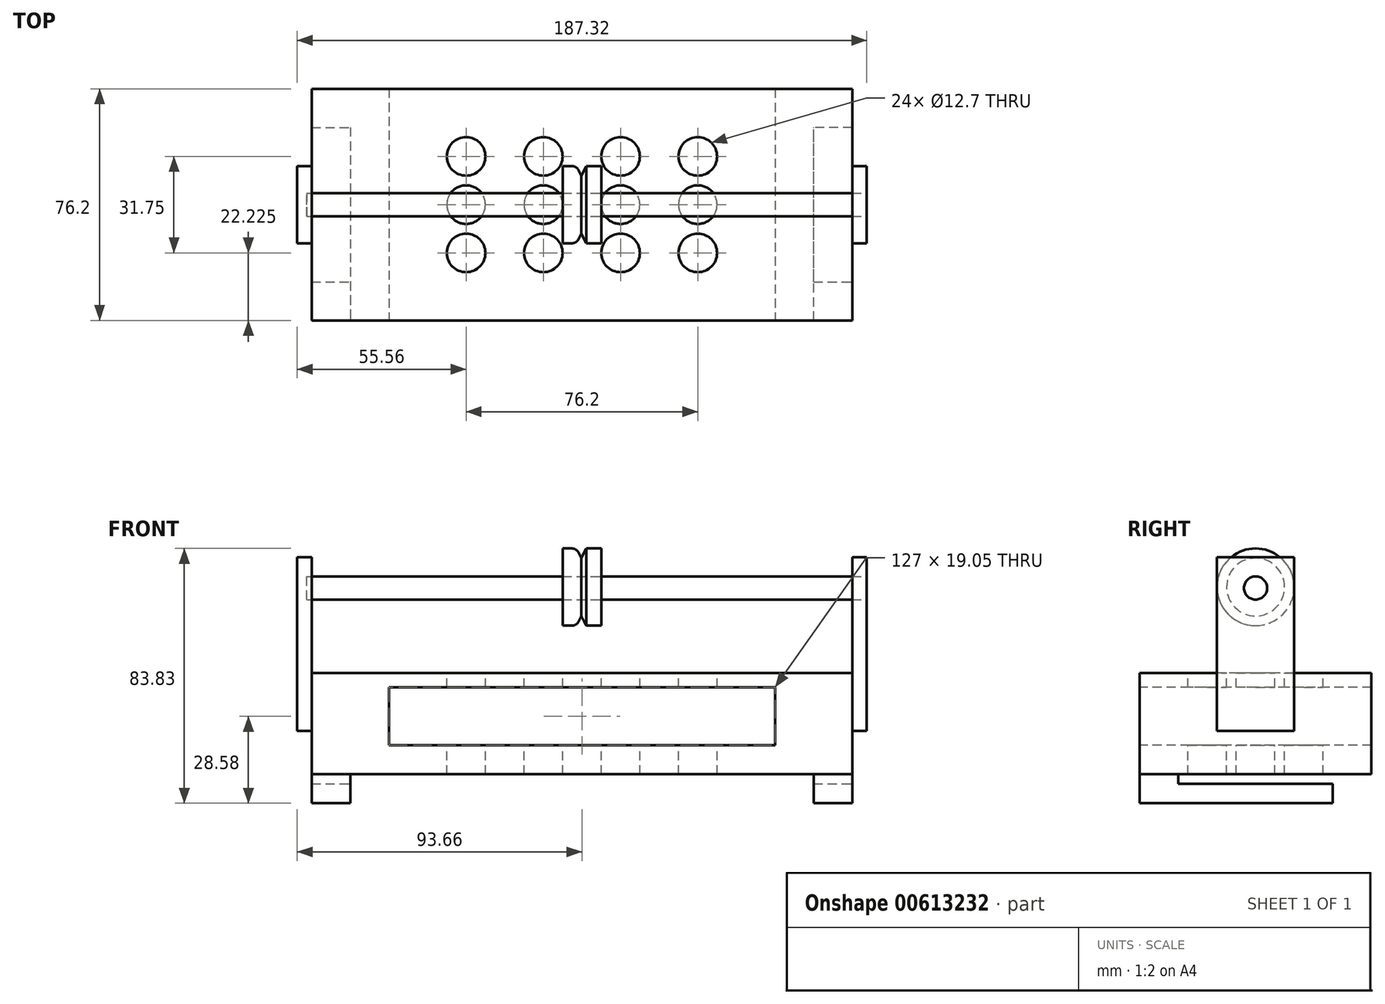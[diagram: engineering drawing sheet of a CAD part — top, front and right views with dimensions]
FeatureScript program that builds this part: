
annotation { "Feature Type Name" : "Feature", "Feature Type Description" : "" }
export const myFeature = defineFeature(function(context is Context, id is Id, definition is map)
    precondition{}
    {
        {
            var Q0;
            Q0=qCreatedBy(makeId("Front.planeOp"),FACE);
            var sketch = newSketch(context, id + "F0", { "sketchPlane" : qUnion([Q0])});
            skLineSegment(sketch, "E0", {"start": v(0, 0) * mm, "end": v(0, 33.34) * mm});
            skLineSegment(sketch, "E1", {"start": v(0, 33.34) * mm, "end": v(177.8, 33.34) * mm});
            skLineSegment(sketch, "E2", {"start": v(177.8, 33.34) * mm, "end": v(177.8, 0) * mm});
            skLineSegment(sketch, "E3", {"start": v(25.4, 28.58) * mm, "end": v(152.4, 28.58) * mm});
            skLineSegment(sketch, "E4", {"start": v(0, 0) * mm, "end": v(177.8, 0) * mm});
            skLineSegment(sketch, "E5", {"start": v(0, 9.52) * mm, "end": v(177.8, 9.53) * mm});
            skLineSegment(sketch, "E6", {"start": v(25.4, 28.58) * mm, "end": v(25.4, 9.52) * mm});
            skLineSegment(sketch, "E7", {"start": v(152.4, 28.58) * mm, "end": v(152.4, 9.53) * mm});
            skSolve(sketch);
        }
        {
            var Q0;
            {var subQ1=sQuery(id+"F0.wireOp",EDGE,"E1");Q0=makeQuery(id+"F0.imprint","IMPRINT",FACE,{"disambiguationData":[TD([[makeQuery(id+"F0.imprint","IMPRINT",EDGE,{"derivedFrom":subQ1}),-1.0]])]});}
            var Q1;
            {var subQ4=sQuery(id+"F0.wireOp",EDGE,"E4");Q1=makeQuery(id+"F0.imprint","IMPRINT",FACE,{"disambiguationData":[TD([[makeQuery(id+"F0.imprint","IMPRINT",EDGE,{"derivedFrom":subQ4}),1.0]])]});}
            var Q2;
            Q2=makeQuery(id+"F0.imprint","IMPRINT",FACE,{"disambiguationData":[TD([[makeQuery(id+"F0.imprint","IMPRINT",EDGE,{"derivedFrom":sQuery(id+"F0.wireOp",EDGE,"E3")}),-1.0]])]});
            extrude(context, id + "F1", {"entities" : qUnion([Q0, Q1, Q2]), "oppositeDirection" : true, "depth" : 76.2 * mm, "offsetDistance" : 25.4 * mm});
        }
        {
            var Q0;
            Q0=makeQuery(id+"F0.imprint","IMPRINT",FACE,{"disambiguationData":[TD([[makeQuery(id+"F0.imprint","IMPRINT",EDGE,{"derivedFrom":sQuery(id+"F0.wireOp",EDGE,"E3")}),-1.0]])]});
            extrude(context, id + "F2", {"entities" : qUnion([Q0]), "operationType" : NewBodyOperationType.REMOVE, "oppositeDirection" : true, "depth" : 76.2 * mm, "offsetDistance" : 25.4 * mm});
        }
        {
            var Q0;
            Q0=makeQuery(id+"F1.opExtrude","SWEPT_FACE",FACE,{"disambiguationData":[OSD([sQuery(id+"F0.wireOp",EDGE,"E2")])]});
            var sketch = newSketch(context, id + "F3", { "sketchPlane" : qUnion([Q0])});
            skLineSegment(sketch, "E8", {"start": v(0, 33.34) * mm, "end": v(25.4, 33.34) * mm});
            skLineSegment(sketch, "E9", {"start": v(76.2, 33.34) * mm, "end": v(50.8, 33.34) * mm});
            skLineSegment(sketch, "E10", {"start": v(50.8, 33.34) * mm, "end": v(50.8, 71.44) * mm});
            skLineSegment(sketch, "E11", {"start": v(50.8, 71.44) * mm, "end": v(25.4, 71.44) * mm});
            skLineSegment(sketch, "E12", {"start": v(25.4, 71.44) * mm, "end": v(25.4, 33.34) * mm});
            skLineSegment(sketch, "E13", {"start": v(25.4, 33.34) * mm, "end": v(25.4, 14.29) * mm});
            skLineSegment(sketch, "E14", {"start": v(25.4, 14.29) * mm, "end": v(50.8, 14.29) * mm});
            skLineSegment(sketch, "E15", {"start": v(50.8, 14.29) * mm, "end": v(50.8, 33.34) * mm});
            skSolve(sketch);
        }
        {
            var Q0;
            {var subQ0=sQuery(id+"F3.wireOp",EDGE,"E13");Q0=makeQuery(id+"F3.imprint","IMPRINT",FACE,{"disambiguationData":[TD([[makeQuery(id+"F3.imprint","IMPRINT",EDGE,{"derivedFrom":subQ0}),1.0]])]});}
            var Q1;
            {var subQ0=sQuery(id+"F3.wireOp",EDGE,"E10");Q1=makeQuery(id+"F3.imprint","IMPRINT",FACE,{"disambiguationData":[TD([[makeQuery(id+"F3.imprint","IMPRINT",EDGE,{"derivedFrom":subQ0}),1.0]])]});}
            extrude(context, id + "F4", {"entities" : qUnion([Q0, Q1]), "operationType" : NewBodyOperationType.ADD, "depth" : 4.76 * mm, "offsetDistance" : 25.4 * mm});
        }
        {
            var Q0;
            Q0=makeQuery(id+"F1.opExtrude","SWEPT_FACE",FACE,{"disambiguationData":[OSD([sQuery(id+"F0.wireOp",EDGE,"E0")])]});
            var sketch = newSketch(context, id + "F5", { "sketchPlane" : qUnion([Q0])});
            skLineSegment(sketch, "E16", {"start": v(-76.2, 33.34) * mm, "end": v(-50.8, 33.34) * mm});
            skLineSegment(sketch, "E17", {"start": v(-50.8, 33.34) * mm, "end": v(-50.8, 71.44) * mm});
            skLineSegment(sketch, "E18", {"start": v(-50.8, 71.44) * mm, "end": v(-25.4, 71.44) * mm});
            skLineSegment(sketch, "E19", {"start": v(-25.4, 71.44) * mm, "end": v(-25.4, 33.34) * mm});
            skLineSegment(sketch, "E20", {"start": v(-25.4, 33.34) * mm, "end": v(0, 33.34) * mm});
            skLineSegment(sketch, "E21", {"start": v(-50.8, 33.34) * mm, "end": v(-50.8, 14.29) * mm});
            skLineSegment(sketch, "E22", {"start": v(-50.8, 14.29) * mm, "end": v(-25.4, 14.29) * mm});
            skLineSegment(sketch, "E23", {"start": v(-25.4, 14.29) * mm, "end": v(-25.4, 33.34) * mm});
            skSolve(sketch);
        }
        {
            var Q0;
            {var subQ0=sQuery(id+"F5.wireOp",EDGE,"E17");Q0=makeQuery(id+"F5.imprint","IMPRINT",FACE,{"disambiguationData":[TD([[makeQuery(id+"F5.imprint","IMPRINT",EDGE,{"derivedFrom":subQ0}),-1.0]])]});}
            var Q1;
            {var subQ0=sQuery(id+"F5.wireOp",EDGE,"E21");Q1=makeQuery(id+"F5.imprint","IMPRINT",FACE,{"disambiguationData":[TD([[makeQuery(id+"F5.imprint","IMPRINT",EDGE,{"derivedFrom":subQ0}),1.0]])]});}
            extrude(context, id + "F6", {"entities" : qUnion([Q0, Q1]), "operationType" : NewBodyOperationType.ADD, "depth" : 4.76 * mm, "offsetDistance" : 25.4 * mm});
        }
        {
            var Q0;
            Q0=makeQuery(id+"F1.opExtrude","SWEPT_FACE",FACE,{"disambiguationData":[OSD([sQuery(id+"F0.wireOp",EDGE,"E1")])]});
            var sketch = newSketch(context, id + "F7", { "sketchPlane" : qUnion([Q0])});
            skLineSegment(sketch, "E24", {"start": v(0, 0) * mm, "end": v(0, 76.2) * mm});
            skLineSegment(sketch, "E25", {"start": v(177.8, 76.2) * mm, "end": v(177.8, 0) * mm});
            skCircle(sketch, "E26", {"center": v(50.8, 53.98) * mm, "radius": 6.35 * mm});
            skCircle(sketch, "E27", {"center": v(50.8, 38.1) * mm, "radius": 6.35 * mm});
            skCircle(sketch, "E28", {"center": v(50.8, 22.22) * mm, "radius": 6.35 * mm});
            skCircle(sketch, "E29", {"center": v(76.2, 38.1) * mm, "radius": 6.35 * mm});
            skCircle(sketch, "E30", {"center": v(76.2, 53.98) * mm, "radius": 6.35 * mm});
            skCircle(sketch, "E31", {"center": v(76.2, 22.22) * mm, "radius": 6.35 * mm});
            skCircle(sketch, "E32", {"center": v(101.6, 38.1) * mm, "radius": 6.35 * mm});
            skCircle(sketch, "E33", {"center": v(101.6, 53.98) * mm, "radius": 6.35 * mm});
            skCircle(sketch, "E34", {"center": v(101.6, 22.22) * mm, "radius": 6.35 * mm});
            skCircle(sketch, "E35", {"center": v(127, 22.22) * mm, "radius": 6.35 * mm});
            skCircle(sketch, "E36", {"center": v(127, 53.98) * mm, "radius": 6.35 * mm});
            skCircle(sketch, "E37", {"center": v(127, 38.1) * mm, "radius": 6.35 * mm});
            skSolve(sketch);
        }
        {
            var Q0;
            Q0=makeQuery(id+"F7.imprint","IMPRINT",FACE,{"disambiguationData":[TD([[makeQuery(id+"F7.imprint","IMPRINT",EDGE,{"derivedFrom":sQuery(id+"F7.wireOp",EDGE,"E26")}),1.0]])]});
            var Q1;
            Q1=makeQuery(id+"F7.imprint","IMPRINT",FACE,{"disambiguationData":[TD([[makeQuery(id+"F7.imprint","IMPRINT",EDGE,{"derivedFrom":sQuery(id+"F7.wireOp",EDGE,"E27")}),1.0]])]});
            var Q2;
            Q2=makeQuery(id+"F7.imprint","IMPRINT",FACE,{"disambiguationData":[TD([[makeQuery(id+"F7.imprint","IMPRINT",EDGE,{"derivedFrom":sQuery(id+"F7.wireOp",EDGE,"E28")}),1.0]])]});
            var Q3;
            Q3=makeQuery(id+"F7.imprint","IMPRINT",FACE,{"disambiguationData":[TD([[makeQuery(id+"F7.imprint","IMPRINT",EDGE,{"derivedFrom":sQuery(id+"F7.wireOp",EDGE,"E31")}),1.0]])]});
            var Q4;
            Q4=makeQuery(id+"F7.imprint","IMPRINT",FACE,{"disambiguationData":[TD([[makeQuery(id+"F7.imprint","IMPRINT",EDGE,{"derivedFrom":sQuery(id+"F7.wireOp",EDGE,"E29")}),1.0]])]});
            var Q5;
            Q5=makeQuery(id+"F7.imprint","IMPRINT",FACE,{"disambiguationData":[TD([[makeQuery(id+"F7.imprint","IMPRINT",EDGE,{"derivedFrom":sQuery(id+"F7.wireOp",EDGE,"E30")}),1.0]])]});
            var Q6;
            Q6=makeQuery(id+"F7.imprint","IMPRINT",FACE,{"disambiguationData":[TD([[makeQuery(id+"F7.imprint","IMPRINT",EDGE,{"derivedFrom":sQuery(id+"F7.wireOp",EDGE,"E33")}),1.0]])]});
            var Q7;
            Q7=makeQuery(id+"F7.imprint","IMPRINT",FACE,{"disambiguationData":[TD([[makeQuery(id+"F7.imprint","IMPRINT",EDGE,{"derivedFrom":sQuery(id+"F7.wireOp",EDGE,"E32")}),1.0]])]});
            var Q8;
            Q8=makeQuery(id+"F7.imprint","IMPRINT",FACE,{"disambiguationData":[TD([[makeQuery(id+"F7.imprint","IMPRINT",EDGE,{"derivedFrom":sQuery(id+"F7.wireOp",EDGE,"E34")}),1.0]])]});
            var Q9;
            Q9=makeQuery(id+"F7.imprint","IMPRINT",FACE,{"disambiguationData":[TD([[makeQuery(id+"F7.imprint","IMPRINT",EDGE,{"derivedFrom":sQuery(id+"F7.wireOp",EDGE,"E35")}),1.0]])]});
            var Q10;
            Q10=makeQuery(id+"F7.imprint","IMPRINT",FACE,{"disambiguationData":[TD([[makeQuery(id+"F7.imprint","IMPRINT",EDGE,{"derivedFrom":sQuery(id+"F7.wireOp",EDGE,"E37")}),1.0]])]});
            var Q11;
            Q11=makeQuery(id+"F7.imprint","IMPRINT",FACE,{"disambiguationData":[TD([[makeQuery(id+"F7.imprint","IMPRINT",EDGE,{"derivedFrom":sQuery(id+"F7.wireOp",EDGE,"E36")}),1.0]])]});
            extrude(context, id + "F8", {"entities" : qUnion([Q0, Q1, Q2, Q3, Q4, Q5, Q6, Q7, Q8, Q9, Q10, Q11]), "operationType" : NewBodyOperationType.REMOVE, "oppositeDirection" : true, "depth" : 34.3 * mm, "offsetDistance" : 25.4 * mm});
        }
        {
            var Q0;
            Q0=makeQuery(id+"F4.opExtrude","CAP_FACE",FACE,{"disambiguationData":[OSD([sQuery(id+"F3.wireOp",EDGE,"E10"),sQuery(id+"F3.wireOp",EDGE,"E11"),sQuery(id+"F3.wireOp",EDGE,"E12"),sQuery(id+"F3.wireOp",EDGE,"E13"),sQuery(id+"F3.wireOp",EDGE,"E14"),sQuery(id+"F3.wireOp",EDGE,"E15")])],"isStart":false});
            var sketch = newSketch(context, id + "F9", { "sketchPlane" : qUnion([Q0])});
            skCircle(sketch, "E38", {"center": v(38.1, 61.28) * mm, "radius": 3.81 * mm});
            skSolve(sketch);
        }
        {
            var Q0;
            Q0=makeQuery(id+"F9.imprint","IMPRINT",FACE,{"disambiguationData":[TD([[makeQuery(id+"F9.imprint","IMPRINT",EDGE,{"derivedFrom":sQuery(id+"F9.wireOp",EDGE,"E38")}),1.0]])]});
            extrude(context, id + "F10", {"entities" : qUnion([Q0]), "oppositeDirection" : true, "depth" : 184.15 * mm, "offsetDistance" : 25.4 * mm});
        }
        {
            var Q0;
            Q0=makeQuery(id+"F1.opExtrude","SWEPT_FACE",FACE,{"disambiguationData":[OSD([sQuery(id+"F0.wireOp",EDGE,"E4")])]});
            var sketch = newSketch(context, id + "F11", { "sketchPlane" : qUnion([Q0])});
            skLineSegment(sketch, "E39", {"start": v(0, 0) * mm, "end": v(0, -12.7) * mm});
            skLineSegment(sketch, "E40", {"start": v(0, -12.7) * mm, "end": v(12.7, -12.7) * mm});
            skLineSegment(sketch, "E41", {"start": v(12.7, -12.7) * mm, "end": v(12.7, 0) * mm});
            skLineSegment(sketch, "E42", {"start": v(12.7, 0) * mm, "end": v(0, 0) * mm});
            skLineSegment(sketch, "E43", {"start": v(177.8, 0) * mm, "end": v(165.1, 0) * mm});
            skLineSegment(sketch, "E44", {"start": v(165.1, 0) * mm, "end": v(165.1, -12.7) * mm});
            skLineSegment(sketch, "E45", {"start": v(165.1, -12.7) * mm, "end": v(177.8, -12.7) * mm});
            skLineSegment(sketch, "E46", {"start": v(177.8, -12.7) * mm, "end": v(177.8, 0) * mm});
            skSolve(sketch);
        }
        {
            var Q0;
            Q0=makeQuery(id+"F11.imprint","IMPRINT",FACE,{"disambiguationData":[TD([[makeQuery(id+"F11.imprint","IMPRINT",EDGE,{"derivedFrom":sQuery(id+"F11.wireOp",EDGE,"E39")}),-1.0]])]});
            var Q1;
            Q1=makeQuery(id+"F11.imprint","IMPRINT",FACE,{"disambiguationData":[TD([[makeQuery(id+"F11.imprint","IMPRINT",EDGE,{"derivedFrom":sQuery(id+"F11.wireOp",EDGE,"E43")}),-1.0]])]});
            extrude(context, id + "F12", {"entities" : qUnion([Q0, Q1]), "depth" : 3.17 * mm, "offsetDistance" : 25.4 * mm});
        }
        {
            var Q0;
            Q0=makeQuery(id+"F12.opExtrude","CAP_FACE",FACE,{"disambiguationData":[OSD([sQuery(id+"F11.wireOp",EDGE,"E39"),sQuery(id+"F11.wireOp",EDGE,"E40"),sQuery(id+"F11.wireOp",EDGE,"E41"),sQuery(id+"F11.wireOp",EDGE,"E42")])],"isStart":false});
            var sketch = newSketch(context, id + "F13", { "sketchPlane" : qUnion([Q0])});
            skLineSegment(sketch, "E47", {"start": v(0, 0) * mm, "end": v(0, -63.5) * mm});
            skLineSegment(sketch, "E48", {"start": v(0, -63.5) * mm, "end": v(12.7, -63.5) * mm});
            skLineSegment(sketch, "E49", {"start": v(12.7, -63.5) * mm, "end": v(12.7, 0) * mm});
            skLineSegment(sketch, "E50", {"start": v(12.7, 0) * mm, "end": v(0, 0) * mm});
            skSolve(sketch);
        }
        {
            var Q0;
            {var subQ2=sQuery(id+"F13.wireOp",EDGE,"E48");Q0=makeQuery(id+"F13.imprint","IMPRINT",FACE,{"disambiguationData":[TD([[makeQuery(id+"F13.imprint","IMPRINT",EDGE,{"derivedFrom":subQ2}),1.0]])]});}
            var Q1;
            {var subQ0=sQuery(id+"F13.wireOp",EDGE,"E50");Q1=makeQuery(id+"F13.imprint","IMPRINT",FACE,{"disambiguationData":[TD([[makeQuery(id+"F13.imprint","IMPRINT",EDGE,{"derivedFrom":subQ0}),-1.0]])]});}
            extrude(context, id + "F14", {"entities" : qUnion([Q0, Q1]), "operationType" : NewBodyOperationType.ADD, "depth" : 6.35 * mm, "offsetDistance" : 25.4 * mm});
        }
        {
            var Q0;
            Q0=makeQuery(id+"F12.opExtrude","CAP_FACE",FACE,{"disambiguationData":[OSD([sQuery(id+"F11.wireOp",EDGE,"E43"),sQuery(id+"F11.wireOp",EDGE,"E44"),sQuery(id+"F11.wireOp",EDGE,"E45"),sQuery(id+"F11.wireOp",EDGE,"E46")])],"isStart":false});
            var sketch = newSketch(context, id + "F15", { "sketchPlane" : qUnion([Q0])});
            skLineSegment(sketch, "E51", {"start": v(177.8, 0) * mm, "end": v(177.8, -63.5) * mm});
            skLineSegment(sketch, "E52", {"start": v(177.8, -63.5) * mm, "end": v(165.1, -63.5) * mm});
            skLineSegment(sketch, "E53", {"start": v(165.1, -63.5) * mm, "end": v(165.1, 0) * mm});
            skLineSegment(sketch, "E54", {"start": v(165.1, 0) * mm, "end": v(177.8, 0) * mm});
            skSolve(sketch);
        }
        {
            var Q0;
            {var subQ0=sQuery(id+"F15.wireOp",EDGE,"E54");Q0=makeQuery(id+"F15.imprint","IMPRINT",FACE,{"disambiguationData":[TD([[makeQuery(id+"F15.imprint","IMPRINT",EDGE,{"derivedFrom":subQ0}),-1.0]])]});}
            var Q1;
            {var subQ2=sQuery(id+"F15.wireOp",EDGE,"E52");Q1=makeQuery(id+"F15.imprint","IMPRINT",FACE,{"disambiguationData":[TD([[makeQuery(id+"F15.imprint","IMPRINT",EDGE,{"derivedFrom":subQ2}),-1.0]])]});}
            extrude(context, id + "F16", {"entities" : qUnion([Q0, Q1]), "operationType" : NewBodyOperationType.ADD, "depth" : 6.35 * mm, "offsetDistance" : 25.4 * mm});
        }
        {
            var Q0;
            Q0=qCreatedBy(makeId("Right.planeOp"),FACE);
            cPlane(context, id + "F17", {"entities" : qUnion([Q0]), "cplaneType" : CPlaneType.OFFSET, "offset" : 88.9 * mm, "width" : 152.4 * mm, "height" : 152.4 * mm});
        }
        {
            var Q0;
            Q0=qCreatedBy(id+"F17.planeOp",FACE);
            var sketch = newSketch(context, id + "F18", { "sketchPlane" : qUnion([Q0])});
            skCircle(sketch, "E55", {"center": v(38.1, 61.6) * mm, "radius": 12.7 * mm});
            skSolve(sketch);
        }
        {
            var Q0;
            Q0=makeQuery(id+"F18.imprint","IMPRINT",FACE,{"disambiguationData":[TD([[makeQuery(id+"F18.imprint","IMPRINT",EDGE,{"derivedFrom":sQuery(id+"F18.wireOp",EDGE,"E55")}),1.0]])]});
            extrude(context, id + "F19", {"entities" : qUnion([Q0]), "endBound" : BoundingType.SYMMETRIC, "depth" : 12.7 * mm, "offsetDistance" : 25.4 * mm});
        }
        {
            var Q0;
            Q0=qCreatedBy(makeId("Front.planeOp"),FACE);
            cPlane(context, id + "F20", {"entities" : qUnion([Q0]), "cplaneType" : CPlaneType.OFFSET, "offset" : 38.1 * mm, "oppositeDirection" : true, "width" : 152.4 * mm, "height" : 152.4 * mm});
        }
        {
            var Q0;
            Q0=qCreatedBy(id+"F20.planeOp",FACE);
            var sketch = newSketch(context, id + "F21", { "sketchPlane" : qUnion([Q0])});
            skLineSegment(sketch, "E56.0", {"start": v(82.55, 74.3) * mm, "end": v(82.55, 48.9) * mm});
            skLineSegment(sketch, "E57.0", {"start": v(95.25, 74.3) * mm, "end": v(95.25, 48.9) * mm});
            skLineSegment(sketch, "E58", {"start": v(87.12, 74.3) * mm, "end": v(90.3, 74.3) * mm});
            skLineSegment(sketch, "E59", {"start": v(82.55, 61.6) * mm, "end": v(95.25, 61.6) * mm});
            skLineSegment(sketch, "E60", {"start": v(87.12, 74.3) * mm, "end": v(88.7, 71.12) * mm});
            skPoint(sketch, "E60.endSnap0", {"position": v(88.7, 74.3) * mm});
            skLineSegment(sketch, "E61", {"start": v(88.7, 71.12) * mm, "end": v(90.3, 74.3) * mm});
            skSolve(sketch);
        }
        {
            var Q0;
            Q0 = qSketchRegion(id + "F21", true);
            var Q1;
            Q1=sQuery(id+"F21.wireOp",EDGE,"E59");
            revolve(context, id + "F22", {"operationType" : NewBodyOperationType.REMOVE, "entities" : qUnion([Q0]), "axis" : qUnion([Q1]), "revolveType" : RevolveType.FULL, "oppositeDirection" : true});
        }
        {
            var Q0;
            Q0=makeQuery(id+"F22.boolean.opBoolean","COPY",EDGE,{"derivedFrom":makeQuery(id+"F22.opRevolve","SWEPT_EDGE",EDGE,{"disambiguationData":[OSD([sQuery(id+"F21.wireOp",EDGE,"E58"),sQuery(id+"F21.wireOp",EDGE,"E60")])]})});
            var Q1;
            Q1=makeQuery(id+"F22.boolean.opBoolean","COPY",EDGE,{"derivedFrom":makeQuery(id+"F22.opRevolve","SWEPT_EDGE",EDGE,{"disambiguationData":[OSD([sQuery(id+"F21.wireOp",EDGE,"E58"),sQuery(id+"F21.wireOp",EDGE,"E61")])]})});
            fillet(context, id + "F23", {"entities" : qUnion([Q0, Q1]), "radius" : 2.54 * mm, "tangentPropagation" : true, "allowEdgeOverflow" : false});
        }
    });
